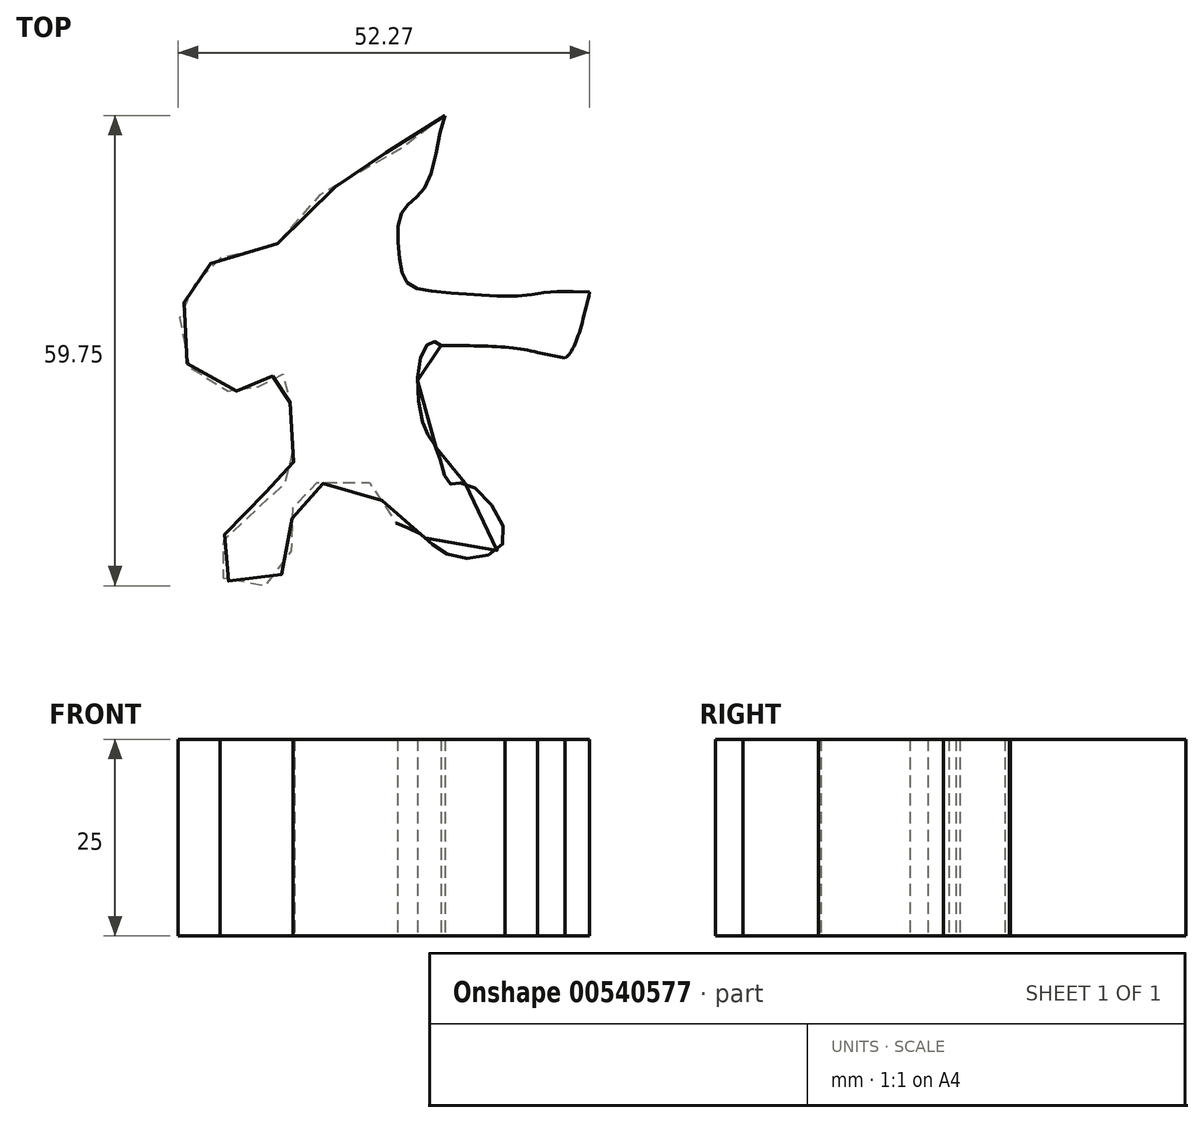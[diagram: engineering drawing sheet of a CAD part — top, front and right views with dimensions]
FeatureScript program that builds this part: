
annotation { "Feature Type Name" : "Feature", "Feature Type Description" : "" }
export const myFeature = defineFeature(function(context is Context, id is Id, definition is map)
    precondition{}
    {
        {
            var Q0;
            Q0=qCreatedBy(makeId("Top.planeOp"),FACE);
            var sketch = newSketch(context, id + "F0", { "sketchPlane" : qUnion([Q0])});
            skFitSpline(sketch, "E0", {"points": [v(-5.95, 49) * mm, v(-11.2, 43.22) * mm, v(-15.91, 41.65) * mm, v(-19.59, 38.5) * mm, v(-23.79, 36.4) * mm, v(-30.08, 29.58) * mm, v(-36.38, 28.53) * mm, v(-38.48, 26.43) * mm, v(-40.05, 24.33) * mm, v(-41.1, 21.7) * mm, v(-41.1, 16.98) * mm, v(-37.43, 12.26) * mm, v(-34.28, 11.74) * mm, v(-32.18, 11.74) * mm, v(-30.6, 12.79) * mm, v(-29.03, 13.84) * mm, v(-27.98, 13.84) * mm, v(-27.46, 11.74) * mm, v(-26.93, 8.59) * mm, v(-26.93, 4.4) * mm, v(-26.93, 0) * mm, v(-29.03, 0) * mm, v(-33.23, -5.05) * mm, v(-35.33, -6.1) * mm, v(-35.85, -9.25) * mm, v(-35.85, -11.87) * mm, v(-32.18, -12.92) * mm, v(-29.03, -12.4) * mm, v(-26.93, -8.2) * mm, v(-26.93, -5.05) * mm, v(-25.88, 0) * mm, v(-22.74, 0) * mm, v(-16.96, 0) * mm, v(-14.34, -4.53) * mm, v(-11.2, -6.1) * mm, v(-6.47, -9.25) * mm, v(0, -7.15) * mm, v(-4.9, 0) * mm, v(-7, 0) * mm, v(-8.57, 4.4) * mm, v(-10.14, 7.02) * mm, v(-10.67, 15.94) * mm, v(-9.1, 18.03) * mm, v(-8.04, 17.5) * mm], "startDerivative": vector(-150.59, -217.02) * mm, "endDerivative": vector(79.38, -65.44) * mm});
            skFitSpline(sketch, "E1", {"points": [v(1.93, 15.94) * mm, v(0, 16.46) * mm], "startDerivative": vector(-1.93, 0.52) * mm, "endDerivative": vector(-1.93, 0.52) * mm});
            skFitSpline(sketch, "E2", {"points": [v(2.45, 16.98) * mm, v(7.7, 15.94) * mm], "startDerivative": vector(5.25, -1.05) * mm, "endDerivative": vector(5.25, -1.05) * mm});
            skFitSpline(sketch, "E3", {"points": [v(10.84, 24.33) * mm, v(5.6, 24.33) * mm, v(1.93, 23.8) * mm, v(-8.04, 24.33) * mm, v(-12.24, 25.38) * mm, v(-13.3, 28.53) * mm, v(-13.3, 33.77) * mm, v(-11.72, 35.87) * mm, v(-9.62, 38.5) * mm, v(-7.59, 46.62) * mm, v(-5.95, 49) * mm], "startDerivative": vector(-53.8, 2.23) * mm, "endDerivative": vector(22.75, 22.04) * mm});
            skFitSpline(sketch, "E4", {"points": [v(10.84, 24.33) * mm, v(7.7, 15.94) * mm, v(4.2, 16.63) * mm, v(-8.04, 17.5) * mm], "startDerivative": vector(-7.45, -32.02) * mm, "endDerivative": vector(-33.5, 0.02) * mm});
            skSolve(sketch);
        }
        {
            var Q0;
            {var subQ0=sQuery(id+"F0.wireOp",EDGE,"E4");var subQ5=sQuery(id+"F0.wireOp",EDGE,"E0");var subQ8=makeQuery(id+"F0.imprint","INTERSECT",VERTEX,{"derivedFrom":[subQ5,subQ0]});Q0=makeQuery(id+"F0.imprint","IMPRINT",FACE,{"disambiguationData":[TD([[makeQuery(id+"F0.imprint","IMPRINT",EDGE,{"disambiguationData":[TD([[subQ8,1.0]])],"derivedFrom":subQ5}),1.0]])]});}
            extrude(context, id + "F1", {"entities" : qUnion([Q0]), "depth" : 25 * mm, "offsetDistance" : 25 * mm});
        }
    });
